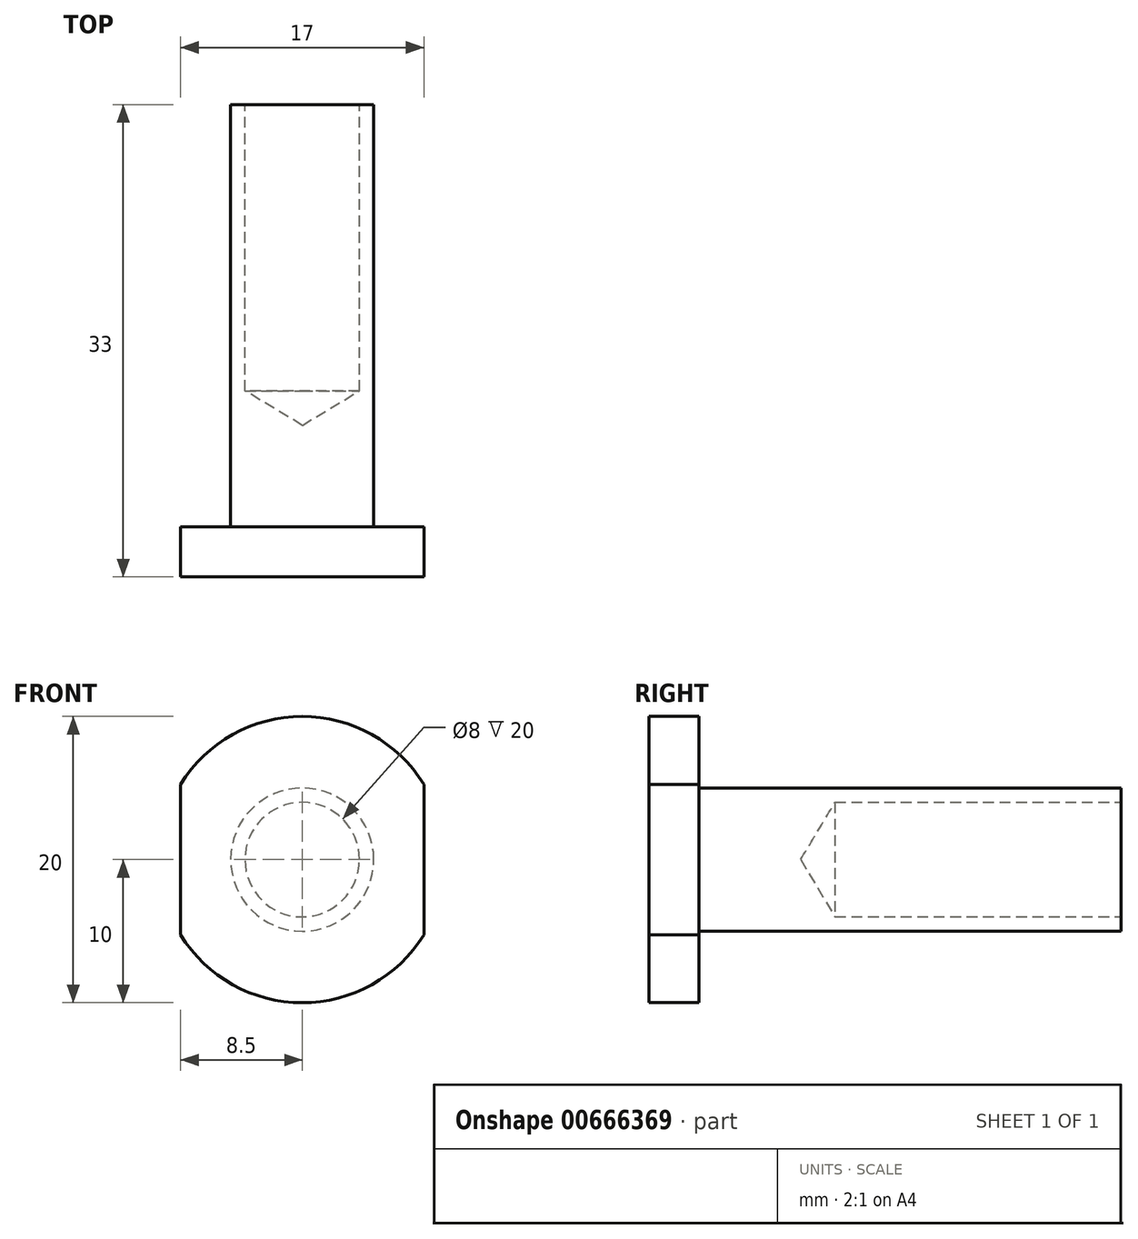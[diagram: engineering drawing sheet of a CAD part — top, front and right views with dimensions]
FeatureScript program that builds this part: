
annotation { "Feature Type Name" : "Feature", "Feature Type Description" : "" }
export const myFeature = defineFeature(function(context is Context, id is Id, definition is map)
    precondition{}
    {
        {
            var Q0;
            Q0=qCreatedBy(makeId("Front.planeOp"),FACE);
            var sketch = newSketch(context, id + "F0", { "sketchPlane" : qUnion([Q0])});
            skCircle(sketch, "E0", {"center": v(0, 0) * mm, "radius": 10 * mm});
            skSolve(sketch);
        }
        {
            var Q0;
            Q0 = qSketchRegion(id + "F0", true);
            extrude(context, id + "F1", {"entities" : qUnion([Q0]), "depth" : 3.5 * mm, "offsetDistance" : 25 * mm});
        }
        {
            var Q0;
            Q0=makeQuery(id+"F1.opExtrude","CAP_FACE",FACE,{"disambiguationData":[OSD([sQuery(id+"F0.wireOp",EDGE,"E0")])],"isStart":true});
            var sketch = newSketch(context, id + "F2", { "sketchPlane" : qUnion([Q0])});
            skCircle(sketch, "E1", {"center": v(0, 0) * mm, "radius": 5 * mm});
            skSolve(sketch);
        }
        {
            var Q0;
            Q0=makeQuery(id+"F2.imprint","IMPRINT",FACE,{"disambiguationData":[TD([[makeQuery(id+"F2.imprint","IMPRINT",EDGE,{"derivedFrom":sQuery(id+"F2.wireOp",EDGE,"E1")}),1.0]])]});
            extrude(context, id + "F3", {"entities" : qUnion([Q0]), "operationType" : NewBodyOperationType.ADD, "depth" : 29.5 * mm, "offsetDistance" : 25 * mm});
        }
        {
            var Q0;
            Q0=makeQuery(id+"F3.opExtrude","CAP_FACE",FACE,{"disambiguationData":[OSD([sQuery(id+"F2.wireOp",EDGE,"E1")])],"isStart":false});
            var sketch = newSketch(context, id + "F4", { "sketchPlane" : qUnion([Q0])});
            skPoint(sketch, "E2", {"position": v(0, 0) * mm});
            skSolve(sketch);
        }
        {
            var Q0;
            Q0=sQuery(id+"F4.wireOp",VERTEX,"E2");
            var Q1;
            Q1=makeQuery(id+"F1.opExtrude","SWEPT_BODY",BODY,{"disambiguationData":[OSD([sQuery(id+"F0.wireOp",EDGE,"E0")])]});
            hole(context, id + "F5", {"style" : HoleStyle.SIMPLE, "endStyle" : HoleEndStyle.BLIND, "holeDiameter" : 8 * mm, "majorDiameter" : 5 * mm, "holeDepth" : 20 * mm, "isTappedThrough" : true, "tappedDepth" : 12 * mm, "tapClearance" : 3, "startFromSketch" : true, "locations" : qUnion([Q0]), "scope" : qUnion([Q1])});
        }
        {
            var Q0;
            Q0=makeQuery(id+"F1.opExtrude","CAP_FACE",FACE,{"disambiguationData":[OSD([sQuery(id+"F0.wireOp",EDGE,"E0")])],"isStart":false});
            var sketch = newSketch(context, id + "F6", { "sketchPlane" : qUnion([Q0])});
            skArc(sketch, "E3", {"start": v(8.5, -5.27) * mm, "mid": v(10, 0) * mm, "end": v(8.5, 5.27) * mm});
            skLineSegment(sketch, "E4", {"start": v(0, 10) * mm, "end": v(0, -10) * mm});
            skLineSegment(sketch, "E5.0", {"start": v(-8.5, 5.27) * mm, "end": v(-8.5, -5.27) * mm});
            skLineSegment(sketch, "E6.MirrorCS", {"start": v(8.5, 5.27) * mm, "end": v(8.5, -5.27) * mm});
            skPoint(sketch, "E7.orphan", {"position": v(-8.5, 10) * mm});
            skPoint(sketch, "E8.orphan", {"position": v(8.5, 10) * mm});
            skPoint(sketch, "E9.orphan", {"position": v(-8.5, -10) * mm});
            skPoint(sketch, "E10.orphan", {"position": v(8.5, -10) * mm});
            skArc(sketch, "E11.trimOffspring", {"start": v(-8.5, 5.27) * mm, "mid": v(-10, 0) * mm, "end": v(-8.5, -5.27) * mm});
            skSolve(sketch);
        }
        {
            var Q0;
            Q0=makeQuery(id+"F6.imprint","IMPRINT",FACE,{"disambiguationData":[TD([[makeQuery(id+"F6.imprint","IMPRINT",EDGE,{"derivedFrom":sQuery(id+"F6.wireOp",EDGE,"E5.0")}),-1.0]])]});
            var Q1;
            Q1=makeQuery(id+"F6.imprint","IMPRINT",FACE,{"disambiguationData":[TD([[makeQuery(id+"F6.imprint","IMPRINT",EDGE,{"derivedFrom":sQuery(id+"F6.wireOp",EDGE,"E3")}),1.0]])]});
            extrude(context, id + "F7", {"entities" : qUnion([Q0, Q1]), "operationType" : NewBodyOperationType.REMOVE, "endBound" : BoundingType.THROUGH_ALL, "oppositeDirection" : true, "depth" : 25 * mm, "offsetDistance" : 25 * mm});
        }
    });
